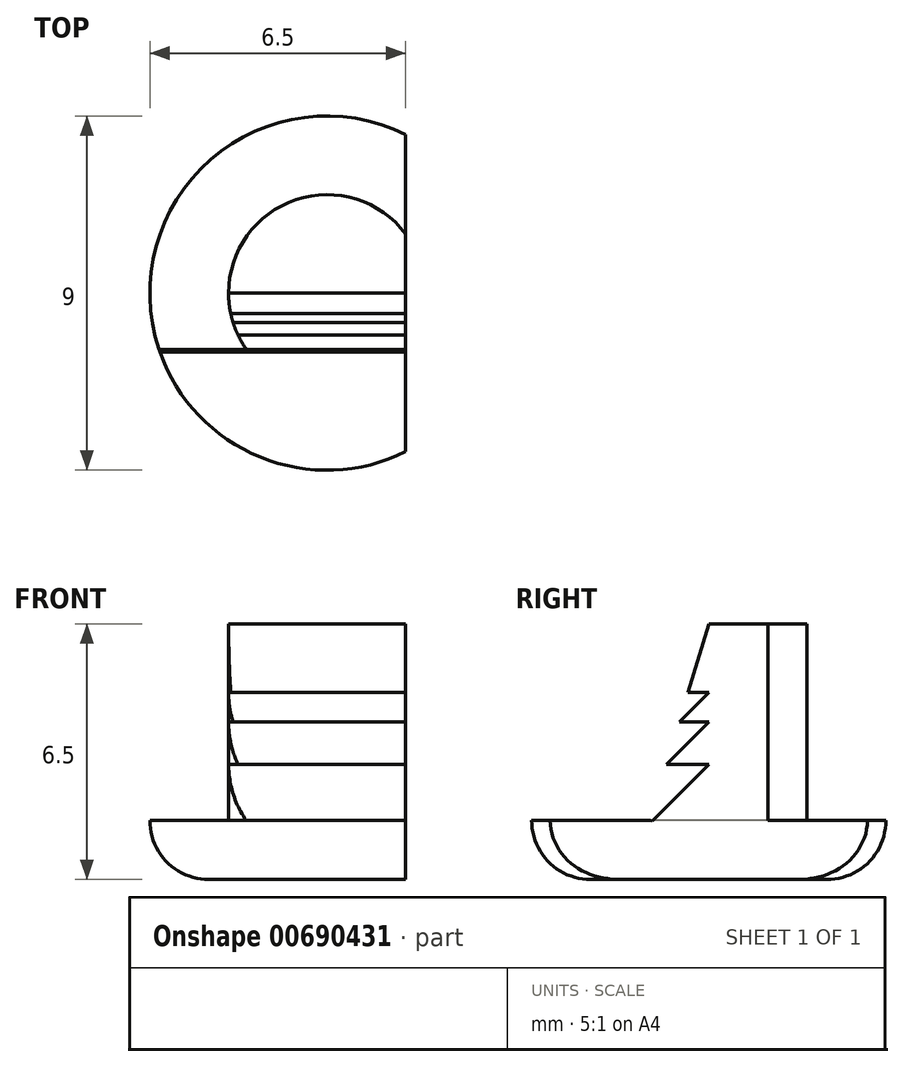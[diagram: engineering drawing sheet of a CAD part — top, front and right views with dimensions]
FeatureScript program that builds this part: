
annotation { "Feature Type Name" : "Feature", "Feature Type Description" : "" }
export const myFeature = defineFeature(function(context is Context, id is Id, definition is map)
    precondition{}
    {
        {
            var Q0;
            Q0=qCreatedBy(makeId("Top.planeOp"),FACE);
            var sketch = newSketch(context, id + "F0", { "sketchPlane" : qUnion([Q0])});
            skCircle(sketch, "E0", {"center": v(0, 0) * mm, "radius": 4.5 * mm});
            skSolve(sketch);
        }
        {
            var Q0;
            Q0 = qSketchRegion(id + "F0", true);
            extrude(context, id + "F1", {"entities" : qUnion([Q0]), "depth" : 1.5 * mm, "offsetDistance" : 25 * mm});
        }
        {
            var Q0;
            Q0=makeQuery(id+"F1.opExtrude","CAP_EDGE",EDGE,{"disambiguationData":[OSD([sQuery(id+"F0.wireOp",EDGE,"E0")])],"isStart":true});
            fillet(context, id + "F2", {"entities" : qUnion([Q0]), "radius" : 1.5 * mm, "tangentPropagation" : true, "allowEdgeOverflow" : false});
        }
        {
            var Q0;
            Q0=makeQuery(id+"F1.opExtrude","CAP_FACE",FACE,{"disambiguationData":[OSD([sQuery(id+"F0.wireOp",EDGE,"E0")])],"isStart":false});
            var sketch = newSketch(context, id + "F3", { "sketchPlane" : qUnion([Q0])});
            skArc(sketch, "E1", {"start": v(2, -1.5) * mm, "mid": v(0, 2.5) * mm, "end": v(-2, -1.5) * mm});
            skLineSegment(sketch, "E2", {"start": v(-2, -1.5) * mm, "end": v(2, -1.5) * mm});
            skSolve(sketch);
        }
        {
            var Q0;
            Q0 = qSketchRegion(id + "F3", true);
            extrude(context, id + "F4", {"entities" : qUnion([Q0]), "operationType" : NewBodyOperationType.ADD, "depth" : 5 * mm, "offsetDistance" : 25 * mm});
        }
        {
            var Q0;
            Q0=makeQuery(id+"F4.opExtrude","CAP_FACE",FACE,{"disambiguationData":[OSD([sQuery(id+"F3.wireOp",EDGE,"E1"),sQuery(id+"F3.wireOp",EDGE,"E2")])],"isStart":false});
            var sketch = newSketch(context, id + "F5", { "sketchPlane" : qUnion([Q0])});
            skLineSegment(sketch, "E3", {"start": v(2, -1.5) * mm, "end": v(2, 6.57) * mm});
            skLineSegment(sketch, "E4", {"start": v(2, 6.57) * mm, "end": v(2, -5.94) * mm});
            skLineSegment(sketch, "E5", {"start": v(6.44, 4.08) * mm, "end": v(5.3, -4.5) * mm});
            skLineSegment(sketch, "E6", {"start": v(5.3, -4.5) * mm, "end": v(2, -5.94) * mm});
            skLineSegment(sketch, "E7", {"start": v(6.44, 4.08) * mm, "end": v(2, 6.57) * mm});
            skSolve(sketch);
        }
        {
            var Q0;
            Q0 = qSketchRegion(id + "F5", true);
            extrude(context, id + "F6", {"entities" : qUnion([Q0]), "operationType" : NewBodyOperationType.REMOVE, "oppositeDirection" : true, "depth" : 25 * mm, "offsetDistance" : 25 * mm});
        }
        {
            var Q0;
            Q0=makeQuery(id+"F6.boolean.opBoolean","COPY",FACE,{"derivedFrom":makeQuery(id+"F6.opExtrude","SWEPT_FACE",FACE,{"disambiguationData":[OSD([sQuery(id+"F5.wireOp",EDGE,"E4")])]})});
            var sketch = newSketch(context, id + "F7", { "sketchPlane" : qUnion([Q0])});
            skLineSegment(sketch, "E8", {"start": v(-1.43, 1.5) * mm, "end": v(-1.5, 1.5) * mm});
            skPoint(sketch, "E9.endSnap0", {"position": v(0, 4) * mm});
            skLineSegment(sketch, "E10", {"start": v(0, 4.75) * mm, "end": v(-0.75, 4) * mm});
            skLineSegment(sketch, "E11", {"start": v(-0.75, 4) * mm, "end": v(0, 4) * mm});
            skLineSegment(sketch, "E12", {"start": v(0, 4) * mm, "end": v(-1.07, 2.93) * mm});
            skLineSegment(sketch, "E13", {"start": v(-1.07, 2.93) * mm, "end": v(0, 2.93) * mm});
            skLineSegment(sketch, "E14", {"start": v(-1.43, 1.5) * mm, "end": v(-1.53, 1.4) * mm});
            skLineSegment(sketch, "E15", {"start": v(0, 4.75) * mm, "end": v(-0.52, 4.75) * mm});
            skPoint(sketch, "E16.orphan", {"position": v(0, 1.4) * mm});
            skPoint(sketch, "E17.orphan", {"position": v(0, 1.5) * mm});
            skLineSegment(sketch, "E18.trimOffspring", {"start": v(-0.52, 4.75) * mm, "end": v(0, 6.5) * mm});
            skLineSegment(sketch, "E19", {"start": v(0, 2.93) * mm, "end": v(-1.43, 1.5) * mm});
            skLineSegment(sketch, "E20", {"start": v(-1.5, 6.5) * mm, "end": v(-1.5, 1.5) * mm});
            skLineSegment(sketch, "E21", {"start": v(-1.5, 6.5) * mm, "end": v(0, 6.5) * mm});
            skSolve(sketch);
        }
        {
            var Q0;
            Q0 = qSketchRegion(id + "F7", true);
            extrude(context, id + "F8", {"entities" : qUnion([Q0]), "operationType" : NewBodyOperationType.REMOVE, "oppositeDirection" : true, "depth" : 25 * mm, "offsetDistance" : 25 * mm});
        }
    });
